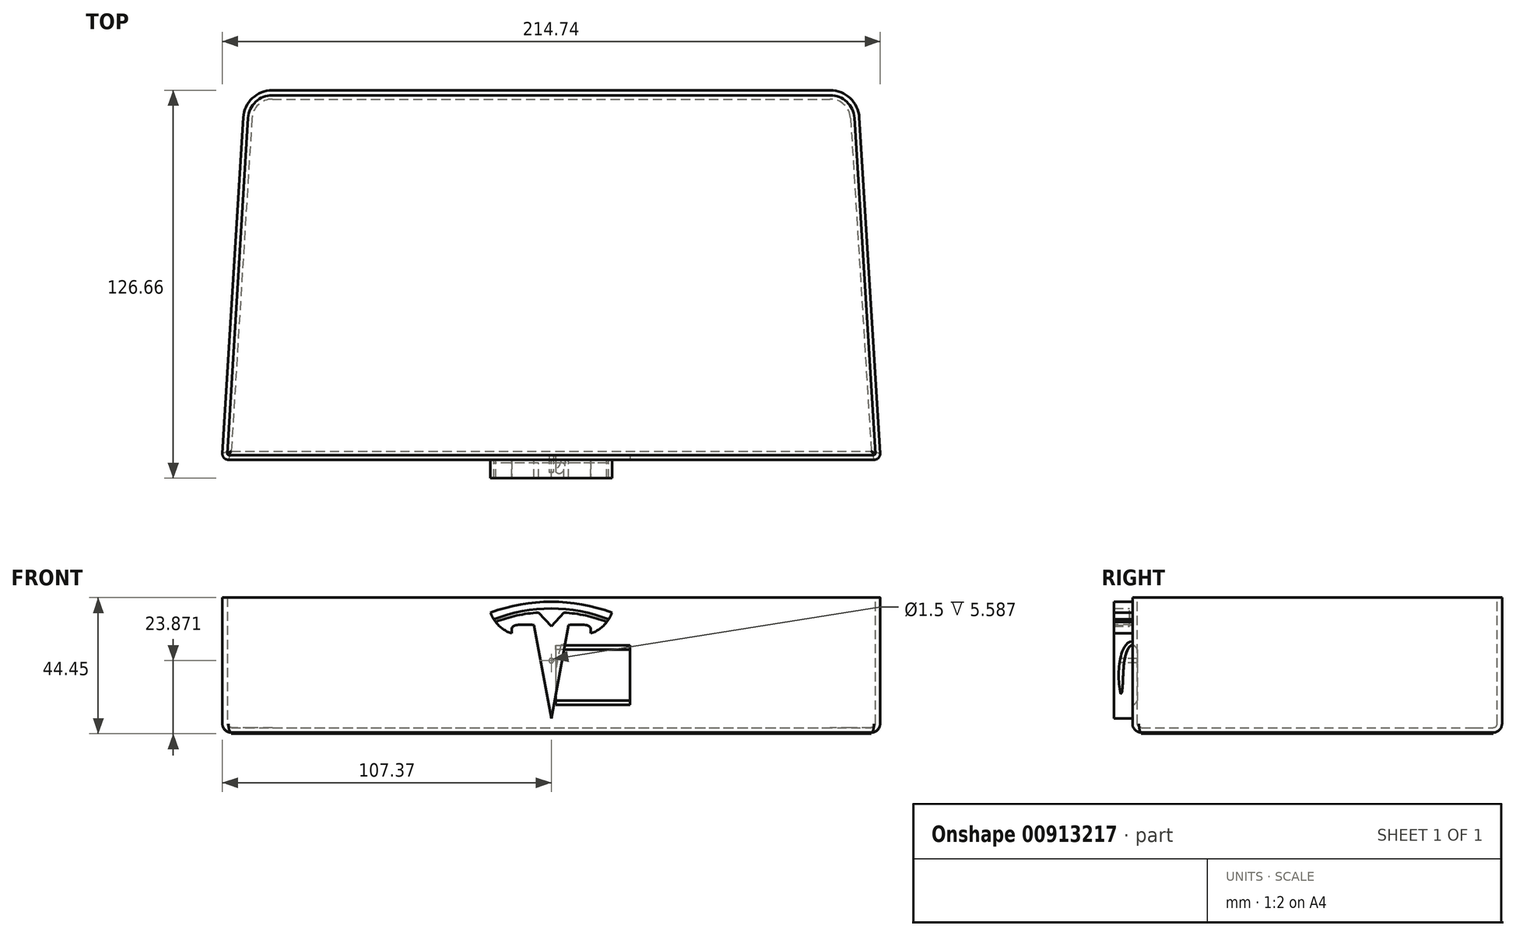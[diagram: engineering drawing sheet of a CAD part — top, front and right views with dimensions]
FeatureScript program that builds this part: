
annotation { "Feature Type Name" : "Feature", "Feature Type Description" : "" }
export const myFeature = defineFeature(function(context is Context, id is Id, definition is map)
    precondition{}
    {
        {
            assignVariable(context, id + "F0", {"name" : "DrawerHeight", "anyValue" : 44.45 * mm});
        }
        {
            assignVariable(context, id + "F1", {"name" : "CornerRadius", "anyValue" : 9.52 * mm});
        }
        {
            assignVariable(context, id + "F2", {"name" : "WallThickness", "anyValue" : 1.59 * mm});
        }
        {
            assignVariable(context, id + "F3", {"name" : "FootThickness", "anyValue" : 0.43 * mm});
        }
        {
            assignVariable(context, id + "F4", {"name" : "BottomRadius", "anyValue" : 2.86 * mm});
        }
        {
            var Q0;
            Q0=qCreatedBy(makeId("Top.planeOp"),FACE);
            var sketch = newSketch(context, id + "F5", { "sketchPlane" : qUnion([Q0])});
            skLineSegment(sketch, "E0.top", {"start": v(-107.5, -60.32) * mm, "end": v(107.5, -60.33) * mm});
            skLineSegment(sketch, "E1", {"start": v(0, 0) * mm, "end": v(0, 122.7) * mm, "construction": true});
            skLineSegment(sketch, "E2", {"start": v(0, 0) * mm, "end": v(154.69, 0) * mm, "construction": true});
            skLineSegment(sketch, "E3", {"start": v(-100, 60.33) * mm, "end": v(100, 60.33) * mm});
            skLineSegment(sketch, "E4", {"start": v(-100, 60.33) * mm, "end": v(-107.5, -60.33) * mm});
            skLineSegment(sketch, "E5", {"start": v(100, 60.33) * mm, "end": v(107.5, -60.33) * mm});
            skSolve(sketch);
        }
        {
            var Q0;
            Q0 = qSketchRegion(id + "F5", true);
            extrude(context, id + "F6", {"entities" : qUnion([Q0]), "depth" : getVariable(context, 'DrawerHeight') - getVariable(context, 'FootThickness'), "offsetDistance" : 25 * mm});
        }
        {
            var Q0;
            Q0=makeQuery(id+"F6.opExtrude","SWEPT_EDGE",EDGE,{"disambiguationData":[OSD([sQuery(id+"F5.wireOp",EDGE,"E0.bottom"),sQuery(id+"F5.wireOp",EDGE,"E0.left")])]});
            var Q1;
            Q1=makeQuery(id+"F6.opExtrude","SWEPT_EDGE",EDGE,{"disambiguationData":[OSD([sQuery(id+"F5.wireOp",EDGE,"E0.bottom"),sQuery(id+"F5.wireOp",EDGE,"E0.right")])]});
            var Q2;
            Q2=makeQuery(id+"F6.opExtrude","SWEPT_EDGE",EDGE,{"disambiguationData":[OSD([sQuery(id+"F5.wireOp",EDGE,"E3"),sQuery(id+"F5.wireOp",EDGE,"E4")])]});
            var Q3;
            Q3=makeQuery(id+"F6.opExtrude","SWEPT_EDGE",EDGE,{"disambiguationData":[OSD([sQuery(id+"F5.wireOp",EDGE,"E3"),sQuery(id+"F5.wireOp",EDGE,"E5")])]});
            fillet(context, id + "F7", {"entities" : qUnion([Q0, Q1, Q2, Q3]), "radius" : getVariable(context, 'CornerRadius'), "tangentPropagation" : true, "allowEdgeOverflow" : false});
        }
        {
            var Q0;
            Q0=makeQuery(id+"F6.opExtrude","SWEPT_EDGE",EDGE,{"disambiguationData":[OSD([sQuery(id+"F5.wireOp",EDGE,"E0.top"),sQuery(id+"F5.wireOp",EDGE,"E4")])]});
            var Q1;
            Q1=makeQuery(id+"F6.opExtrude","SWEPT_EDGE",EDGE,{"disambiguationData":[OSD([sQuery(id+"F5.wireOp",EDGE,"E0.top"),sQuery(id+"F5.wireOp",EDGE,"E5")])]});
            fillet(context, id + "F8", {"entities" : qUnion([Q0, Q1]), "radius" : 2 * mm, "tangentPropagation" : true, "allowEdgeOverflow" : false});
        }
        {
            var Q0;
            Q0=makeQuery(id+"F6.opExtrude","CAP_EDGE",EDGE,{"disambiguationData":[OSD([sQuery(id+"F5.wireOp",EDGE,"E0.top")])],"isStart":true});
            fillet(context, id + "F9", {"entities" : qUnion([Q0]), "radius" : getVariable(context, 'BottomRadius'), "tangentPropagation" : true, "allowEdgeOverflow" : false});
        }
        {
            var Q0;
            Q0=makeQuery(id+"F6.opExtrude","CAP_FACE",FACE,{"disambiguationData":[OSD([sQuery(id+"F5.wireOp",EDGE,"E0.bottom"),sQuery(id+"F5.wireOp",EDGE,"E0.top"),sQuery(id+"F5.wireOp",EDGE,"E0.left"),sQuery(id+"F5.wireOp",EDGE,"E0.right")])],"isStart":false});
            shell(context, id + "F10", {"entities" : qUnion([Q0]), "thickness" : getVariable(context, 'WallThickness')});
        }
        {
            var Q0;
            Q0=makeQuery(id+"F6.opExtrude","CAP_FACE",FACE,{"disambiguationData":[OSD([sQuery(id+"F5.wireOp",EDGE,"E0.bottom"),sQuery(id+"F5.wireOp",EDGE,"E0.top"),sQuery(id+"F5.wireOp",EDGE,"E0.left"),sQuery(id+"F5.wireOp",EDGE,"E0.right")])],"isStart":true});
            extrude(context, id + "F11", {"entities" : qUnion([Q0]), "operationType" : NewBodyOperationType.ADD, "depth" : getVariable(context, 'FootThickness'), "offsetDistance" : 25 * mm});
        }
        {
            var Q0;
            Q0=makeQuery(id+"F6.opExtrude","SWEPT_FACE",FACE,{"disambiguationData":[OSD([sQuery(id+"F5.wireOp",EDGE,"E0.top")])]});
            var sketch = newSketch(context, id + "F12", { "sketchPlane" : qUnion([Q0])});
            skLineSegment(sketch, "E6", {"start": v(0, 44.02) * mm, "end": v(0, 0) * mm, "construction": true});
            skLineSegment(sketch, "E7", {"start": v(-105.37, 23.44) * mm, "end": v(105.37, 23.44) * mm, "construction": true});
            skCircle(sketch, "E8", {"center": v(0, 23.44) * mm, "radius": 0.75 * mm});
            skSolve(sketch);
        }
        {
            var Q0;
            Q0 = qSketchRegion(id + "F12", true);
            extrude(context, id + "F13", {"entities" : qUnion([Q0]), "operationType" : NewBodyOperationType.REMOVE, "oppositeDirection" : true, "depth" : 25 * mm, "offsetDistance" : 25 * mm});
        }
        {
            var Q0;
            Q0=makeQuery(id+"F6.opExtrude","SWEPT_FACE",FACE,{"disambiguationData":[OSD([sQuery(id+"F5.wireOp",EDGE,"E0.top")])]});
            var sketch = newSketch(context, id + "F14", { "sketchPlane" : qUnion([Q0])});
            skFitSpline(sketch, "E9.0.0", {"points": [v(12.86, 32.32) * mm, v(12.72, 34.32) * mm, v(10.91, 35.1) * mm, v(5.67, 35.1) * mm]});
            skLineSegment(sketch, "E9.0.1", {"start": v(5.67, 35.1) * mm, "end": v(0, 4.6) * mm});
            skLineSegment(sketch, "E9.0.2", {"start": v(0, 4.6) * mm, "end": v(-5.67, 35.1) * mm});
            skFitSpline(sketch, "E9.0.3", {"points": [v(-5.67, 35.1) * mm, v(-10.91, 35.1) * mm, v(-12.72, 34.32) * mm, v(-12.86, 32.32) * mm]});
            skArc(sketch, "E9.0.4", {"start": v(-12.86, 32.32) * mm, "mid": v(-15.8, 33.79) * mm, "end": v(-18.16, 36.06) * mm});
            skArc(sketch, "E9.0.5", {"start": v(-18.16, 36.06) * mm, "mid": v(-11.25, 38.18) * mm, "end": v(-4.09, 39.14) * mm});
            skLineSegment(sketch, "E9.0.6", {"start": v(-4.09, 39.14) * mm, "end": v(0, 34.67) * mm});
            skLineSegment(sketch, "E9.0.7", {"start": v(0, 34.67) * mm, "end": v(4.09, 39.14) * mm});
            skArc(sketch, "E9.0.8", {"start": v(18.16, 36.06) * mm, "mid": v(11.25, 38.18) * mm, "end": v(4.09, 39.14) * mm});
            skArc(sketch, "E9.0.9", {"start": v(12.86, 32.32) * mm, "mid": v(15.8, 33.79) * mm, "end": v(18.16, 36.06) * mm});
            skArc(sketch, "E9.1.0", {"start": v(18.75, 36.9) * mm, "mid": v(0, 40.46) * mm, "end": v(-18.75, 36.9) * mm});
            skArc(sketch, "E9.1.1", {"start": v(-18.75, 36.9) * mm, "mid": v(-19.34, 37.99) * mm, "end": v(-19.81, 39.13) * mm});
            skArc(sketch, "E9.1.2", {"start": v(-19.81, 39.13) * mm, "mid": v(0, 42.7) * mm, "end": v(19.81, 39.13) * mm});
            skArc(sketch, "E9.1.3", {"start": v(18.75, 36.9) * mm, "mid": v(19.34, 37.99) * mm, "end": v(19.81, 39.13) * mm});
            skLineSegment(sketch, "E10", {"start": v(0, 4.6) * mm, "end": v(0, 42.7) * mm, "construction": true});
            skSolve(sketch);
        }
        {
            var Q0;
            Q0=makeQuery(id+"F14.imprint","IMPRINT",FACE,{"disambiguationData":[TD([[makeQuery(id+"F14.imprint","IMPRINT",EDGE,{"derivedFrom":sQuery(id+"F14.wireOp",EDGE,"E9.0.0")}),1.0]])]});
            var sketch = newSketch(context, id + "F15", { "sketchPlane" : qUnion([Q0])});
            skArc(sketch, "E11.0", {"start": v(-12.86, 32.32) * mm, "mid": v(-15.8, 33.79) * mm, "end": v(-18.16, 36.06) * mm});
            skArc(sketch, "E11.1", {"start": v(-18.75, 36.9) * mm, "mid": v(-19.34, 37.99) * mm, "end": v(-19.81, 39.13) * mm});
            skArc(sketch, "E11.2", {"start": v(-19.81, 39.13) * mm, "mid": v(0, 42.7) * mm, "end": v(19.81, 39.13) * mm});
            skFitSpline(sketch, "E11.3", {"points": [v(-5.67, 35.1) * mm, v(-10.91, 35.1) * mm, v(-12.72, 34.32) * mm, v(-12.86, 32.32) * mm]});
            skLineSegment(sketch, "E11.4", {"start": v(0, 4.6) * mm, "end": v(-5.67, 35.1) * mm});
            skLineSegment(sketch, "E11.5", {"start": v(5.67, 35.1) * mm, "end": v(0, 4.6) * mm});
            skFitSpline(sketch, "E11.6", {"points": [v(12.86, 32.32) * mm, v(12.72, 34.32) * mm, v(10.91, 35.1) * mm, v(5.67, 35.1) * mm]});
            skArc(sketch, "E11.7", {"start": v(18.75, 36.9) * mm, "mid": v(19.34, 37.99) * mm, "end": v(19.81, 39.13) * mm});
            skArc(sketch, "E11.8", {"start": v(12.86, 32.32) * mm, "mid": v(15.8, 33.79) * mm, "end": v(18.16, 36.06) * mm});
            skLineSegment(sketch, "E12", {"start": v(-18.75, 36.9) * mm, "end": v(-18.16, 36.06) * mm});
            skLineSegment(sketch, "E13", {"start": v(18.16, 36.06) * mm, "end": v(18.75, 36.9) * mm});
            skSolve(sketch);
        }
        {
            var Q0;
            Q0 = qSketchRegion(id + "F15", true);
            extrude(context, id + "F16", {"entities" : qUnion([Q0]), "depth" : 1 * mm, "offsetDistance" : 25 * mm});
        }
        {
            var Q0;
            Q0 = qSketchRegion(id + "F14", true);
            extrude(context, id + "F17", {"entities" : qUnion([Q0]), "operationType" : NewBodyOperationType.ADD, "depth" : 6 * mm, "offsetDistance" : 25 * mm});
        }
        {
            var Q0;
            Q0=qCreatedBy(makeId("Right.planeOp"),FACE);
            cPlane(context, id + "F18", {"entities" : qUnion([Q0]), "cplaneType" : CPlaneType.OFFSET, "offset" : 1.5 * mm, "width" : 150 * mm, "height" : 150 * mm});
        }
        {
            var Q0;
            Q0=qCreatedBy(id+"F18.planeOp",FACE);
            var sketch = newSketch(context, id + "F19", { "sketchPlane" : qUnion([Q0])});
            skLineSegment(sketch, "E14", {"start": v(-60.3, 28.51) * mm, "end": v(-60.3, 9) * mm});
            skEllipse(sketch, "E15", {"center": v(-60.3, 18.75) * mm, "majorRadius": 9.76 * mm, "minorRadius": 3 * mm, "majorAxis": v(0, 1)});
            skSolve(sketch);
        }
        {
            var Q0;
            Q0 = qSketchRegion(id + "F19", true);
            extrude(context, id + "F20", {"entities" : qUnion([Q0]), "operationType" : NewBodyOperationType.REMOVE, "depth" : 24.2 * mm, "offsetDistance" : 25 * mm});
        }
        {
            var Q0;
            Q0=makeQuery(id+"FC4LqFccNEvA3M9_2.1.F20.boolean.opBoolean","INTERSECT",EDGE,{"derivedFrom":[makeQuery(id+"F17.boolean.opBoolean","MERGE",FACE,{"derivedFrom":[makeQuery(id+"F16.opExtrude","SWEPT_FACE",FACE,{"disambiguationData":[OSD([sQuery(id+"F15.wireOp",EDGE,"E11.4")])]}),makeQuery(id+"F17.opExtrude","SWEPT_FACE",FACE,{"disambiguationData":[OSD([sQuery(id+"F14.wireOp",EDGE,"E9.0.2")])]})]}),makeQuery(id+"FC4LqFccNEvA3M9_2.1.F20.opExtrude","CAP_FACE",FACE,{"disambiguationData":[OSD([sQuery(id+"F19.wireOp",EDGE,"E15")])],"isStart":true})]});
            var Q1;
            Q1=makeQuery(id+"FC4LqFccNEvA3M9_2.1.F20.boolean.opBoolean","INTERSECT",EDGE,{"derivedFrom":[makeQuery(id+"F17.boolean.opBoolean","MERGE",FACE,{"derivedFrom":[makeQuery(id+"F16.opExtrude","SWEPT_FACE",FACE,{"disambiguationData":[OSD([sQuery(id+"F15.wireOp",EDGE,"E11.4")])]}),makeQuery(id+"F17.opExtrude","SWEPT_FACE",FACE,{"disambiguationData":[OSD([sQuery(id+"F14.wireOp",EDGE,"E9.0.2")])]})]}),makeQuery(id+"FC4LqFccNEvA3M9_2.1.F20.opExtrude","SWEPT_FACE",FACE,{"disambiguationData":[OSD([sQuery(id+"F19.wireOp",EDGE,"E15")])]})]});
            var Q2;
            Q2=makeQuery(id+"F20.boolean.opBoolean","INTERSECT",EDGE,{"derivedFrom":[makeQuery(id+"F17.boolean.opBoolean","MERGE",FACE,{"derivedFrom":[makeQuery(id+"F16.opExtrude","SWEPT_FACE",FACE,{"disambiguationData":[OSD([sQuery(id+"F15.wireOp",EDGE,"E11.5")])]}),makeQuery(id+"F17.opExtrude","SWEPT_FACE",FACE,{"disambiguationData":[OSD([sQuery(id+"F14.wireOp",EDGE,"E9.0.1")])]})]}),makeQuery(id+"F20.opExtrude","SWEPT_FACE",FACE,{"disambiguationData":[OSD([sQuery(id+"F19.wireOp",EDGE,"E15")])]})]});
            var Q3;
            Q3=makeQuery(id+"F20.boolean.opBoolean","INTERSECT",EDGE,{"derivedFrom":[makeQuery(id+"F17.boolean.opBoolean","MERGE",FACE,{"derivedFrom":[makeQuery(id+"F16.opExtrude","SWEPT_FACE",FACE,{"disambiguationData":[OSD([sQuery(id+"F15.wireOp",EDGE,"E11.5")])]}),makeQuery(id+"F17.opExtrude","SWEPT_FACE",FACE,{"disambiguationData":[OSD([sQuery(id+"F14.wireOp",EDGE,"E9.0.1")])]})]}),makeQuery(id+"F20.opExtrude","CAP_FACE",FACE,{"disambiguationData":[OSD([sQuery(id+"F19.wireOp",EDGE,"E15")])],"isStart":true})]});
            fillet(context, id + "F21", {"entities" : qUnion([Q0, Q1, Q2, Q3]), "radius" : 1.5 * mm, "tangentPropagation" : true, "allowEdgeOverflow" : false});
        }
        {
            var Q0;
            Q0=makeQuery(id+"F16.opExtrude","CAP_FACE",FACE,{"disambiguationData":[OSD([sQuery(id+"F15.wireOp",EDGE,"E11.0"),sQuery(id+"F15.wireOp",EDGE,"E11.1"),sQuery(id+"F15.wireOp",EDGE,"E11.2"),sQuery(id+"F15.wireOp",EDGE,"E11.3"),sQuery(id+"F15.wireOp",EDGE,"E11.4"),sQuery(id+"F15.wireOp",EDGE,"E11.5"),sQuery(id+"F15.wireOp",EDGE,"E11.6"),sQuery(id+"F15.wireOp",EDGE,"E11.7"),sQuery(id+"F15.wireOp",EDGE,"E11.8"),sQuery(id+"F15.wireOp",EDGE,"E12"),sQuery(id+"F15.wireOp",EDGE,"E13")])],"isStart":true});
            var sketch = newSketch(context, id + "F22", { "sketchPlane" : qUnion([Q0])});
            skCircle(sketch, "E16.0", {"center": v(0, 23.44) * mm, "radius": 0.75 * mm});
            skSolve(sketch);
        }
        {
            var Q0;
            Q0 = qSketchRegion(id + "F22", true);
            extrude(context, id + "F23", {"entities" : qUnion([Q0]), "operationType" : NewBodyOperationType.REMOVE, "oppositeDirection" : true, "depth" : 4 * mm, "offsetDistance" : 25 * mm});
        }
    });
